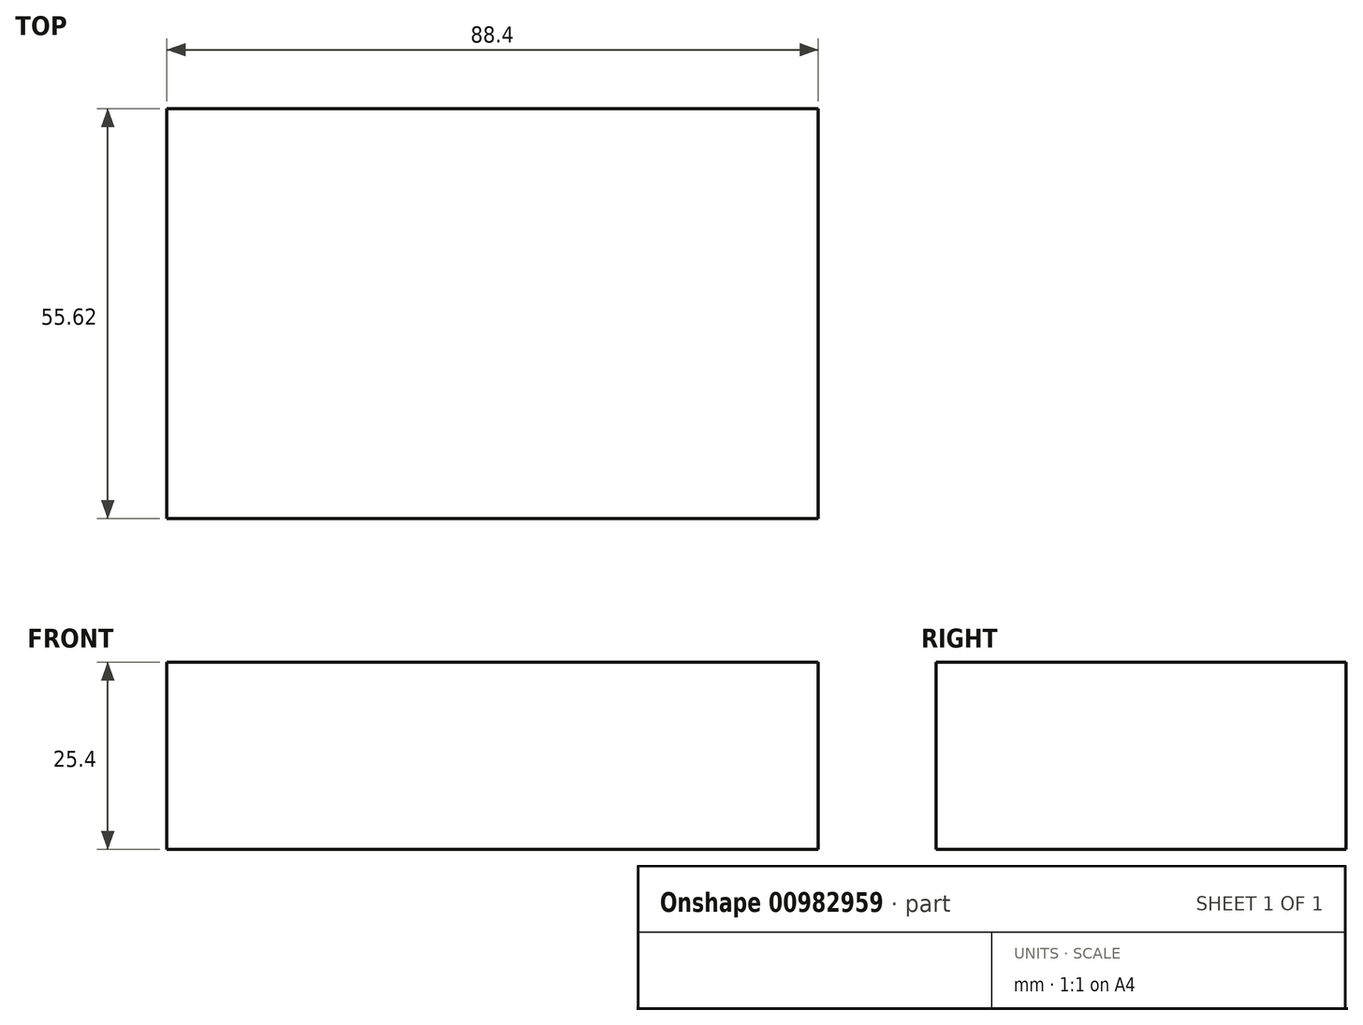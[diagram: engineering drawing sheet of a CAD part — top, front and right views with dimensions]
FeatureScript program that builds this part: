
annotation { "Feature Type Name" : "Feature", "Feature Type Description" : "" }
export const myFeature = defineFeature(function(context is Context, id is Id, definition is map)
    precondition{}
    {
        {
            var Q0;
            Q0=qCreatedBy(makeId("Top.planeOp"),FACE);
            var sketch = newSketch(context, id + "F0", { "sketchPlane" : qUnion([Q0])});
            skLineSegment(sketch, "E0.bottom", {"start": v(-61.71, -27.14) * mm, "end": v(26.7, -27.14) * mm});
            skLineSegment(sketch, "E0.top", {"start": v(-61.71, 28.48) * mm, "end": v(26.7, 28.48) * mm});
            skLineSegment(sketch, "E0.left", {"start": v(-61.71, -27.14) * mm, "end": v(-61.71, 28.48) * mm});
            skLineSegment(sketch, "E0.right", {"start": v(26.7, -27.14) * mm, "end": v(26.7, 28.48) * mm});
            skSolve(sketch);
        }
        {
            var Q0;
            Q0=makeQuery(id+"F0.imprint","IMPRINT",FACE,{"disambiguationData":[TD([[makeQuery(id+"F0.imprint","IMPRINT",EDGE,{"derivedFrom":sQuery(id+"F0.wireOp",EDGE,"E0.bottom")}),1.0]])]});
            extrude(context, id + "F1", {"entities" : qUnion([Q0]), "depth" : 25.4 * mm, "offsetDistance" : 25.4 * mm});
        }
    });
